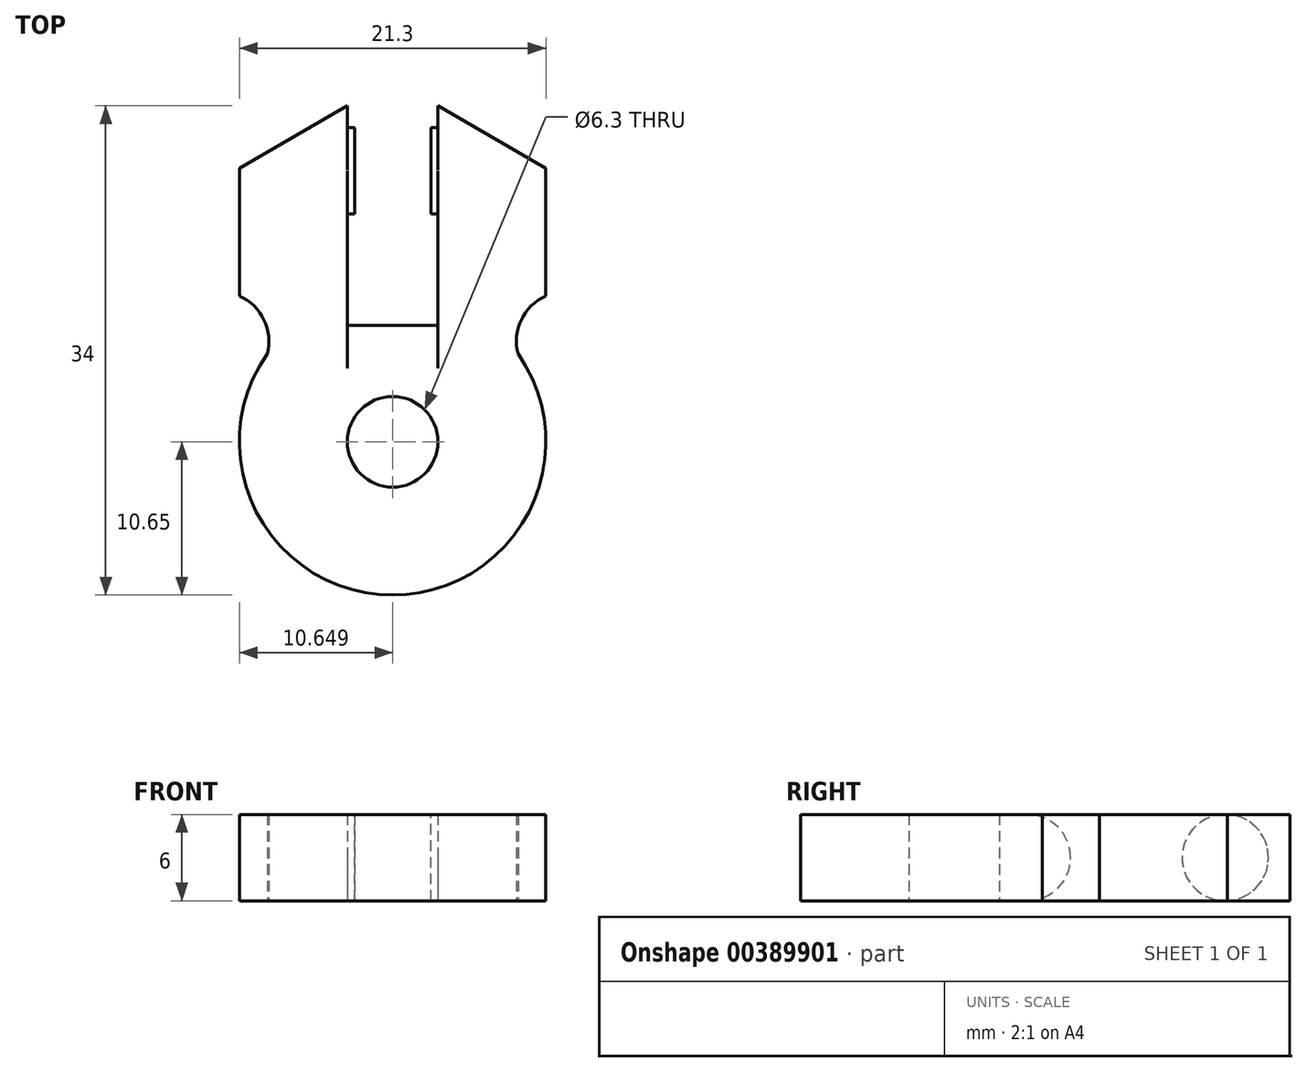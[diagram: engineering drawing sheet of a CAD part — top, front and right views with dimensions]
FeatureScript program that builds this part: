
annotation { "Feature Type Name" : "Feature", "Feature Type Description" : "" }
export const myFeature = defineFeature(function(context is Context, id is Id, definition is map)
    precondition{}
    {
        {
            var Q0;
            Q0=qCreatedBy(makeId("Top.planeOp"),FACE);
            var sketch = newSketch(context, id + "F0", { "sketchPlane" : qUnion([Q0])});
            skCircle(sketch, "E0", {"center": v(27.63, 38) * mm, "radius": 3.15 * mm});
            skArc(sketch, "E1", {"start": v(24.48, 48.16) * mm, "mid": v(27.63, 27.34) * mm, "end": v(30.78, 48.16) * mm});
            skPoint(sketch, "E2", {"position": v(30.78, 46.1) * mm});
            skLineSegment(sketch, "E3", {"start": v(30.78, 46.1) * mm, "end": v(30.78, 61.34) * mm});
            skLineSegment(sketch, "E4", {"start": v(30.78, 46.1) * mm, "end": v(27.63, 46.1) * mm});
            skLineSegment(sketch, "E5.MirrorCS", {"start": v(24.48, 46.1) * mm, "end": v(27.63, 46.1) * mm});
            skLineSegment(sketch, "E6.MirrorCS", {"start": v(24.48, 46.1) * mm, "end": v(24.48, 61.34) * mm});
            skLineSegment(sketch, "E7", {"start": v(16.98, 57) * mm, "end": v(16.98, 48) * mm});
            skLineSegment(sketch, "E8.MirrorCS", {"start": v(38.28, 57) * mm, "end": v(38.28, 48.11) * mm});
            skLineSegment(sketch, "E9", {"start": v(24.48, 61.34) * mm, "end": v(16.98, 57) * mm});
            skLineSegment(sketch, "E10", {"start": v(30.78, 61.34) * mm, "end": v(38.28, 57) * mm});
            skPoint(sketch, "E11.MirrorCS.end.orphan", {"position": v(38.28, 57) * mm});
            skPoint(sketch, "E12.MirrorCS.start.orphan", {"position": v(30.78, 61.34) * mm});
            skArc(sketch, "E13", {"start": v(38.28, 48.11) * mm, "mid": v(36.57, 46.47) * mm, "end": v(36.35, 44.11) * mm});
            skArc(sketch, "E14.MirrorCS", {"start": v(16.98, 48.11) * mm, "mid": v(18.7, 46.47) * mm, "end": v(18.91, 44.11) * mm});
            skSolve(sketch);
        }
        {
            var Q0;
            Q0=qSketchRegion(id+"F0",true);
            extrude(context, id + "F1", {"entities" : qUnion([Q0]), "depth" : 6 * mm});
        }
        {
            var Q0;
            Q0=qCreatedBy(makeId("Right.planeOp"),FACE);
            var sketch = newSketch(context, id + "F2", { "sketchPlane" : qUnion([Q0])});
            skLineSegment(sketch, "E15", {"start": v(61.34, 6) * mm, "end": v(61.34, 0) * mm});
            skLineSegment(sketch, "E16", {"start": v(61.34, 0) * mm, "end": v(57, 0) * mm});
            skLineSegment(sketch, "E17", {"start": v(61.34, 3) * mm, "end": v(59.84, 3) * mm});
            skLineSegment(sketch, "E18", {"start": v(59.84, 3) * mm, "end": v(56.84, 3) * mm});
            skCircle(sketch, "E19", {"center": v(56.84, 3) * mm, "radius": 3 * mm});
            skSolve(sketch);
        }
        {
            var Q0;
            Q0=qSketchRegion(id+"F2",true);
            extrude(context, id + "F3", {"entities" : qUnion([Q0]), "operationType" : NewBodyOperationType.ADD, "depth" : 31 * mm, "hasSecondDirection" : true, "secondDirectionOppositeDirection" : false, "secondDirectionDepth" : 22.4 * mm});
        }
        {
            var Q0;
            Q0=qCreatedBy(makeId("Front.planeOp"),FACE);
            var sketch = newSketch(context, id + "F4", { "sketchPlane" : qUnion([Q0])});
            skLineSegment(sketch, "E20", {"start": v(30.28, 3) * mm, "end": v(30.28, 6.74) * mm});
            skLineSegment(sketch, "E21", {"start": v(30.28, 6.74) * mm, "end": v(24.98, 6.74) * mm});
            skLineSegment(sketch, "E22", {"start": v(24.98, 6.74) * mm, "end": v(24.98, -0.66) * mm});
            skLineSegment(sketch, "E23", {"start": v(24.98, -0.66) * mm, "end": v(30.28, -0.66) * mm});
            skLineSegment(sketch, "E24", {"start": v(30.28, -0.66) * mm, "end": v(30.28, 6.74) * mm});
            skPoint(sketch, "E25.MirrorCS.end.orphan", {"position": v(24.98, 3) * mm});
            skSolve(sketch);
        }
        {
            var Q0;
            {var subQ0=sQuery(id+"F4.wireOp",EDGE,"E21");Q0=makeQuery(id+"F4.imprint","IMPRINT",FACE,{"disambiguationData":[TD([[makeQuery(id+"F4.imprint","IMPRINT",EDGE,{"derivedFrom":subQ0}),1.0]])]});}
            extrude(context, id + "F5", {"entities" : qUnion([Q0]), "operationType" : NewBodyOperationType.REMOVE, "oppositeDirection" : true, "depth" : 63.7 * mm, "hasSecondDirection" : true, "secondDirectionOppositeDirection" : true, "secondDirectionDepth" : 52.7 * mm});
        }
        {
            var Q0;
            Q0=makeQuery(id+"F1.opExtrude","CAP_EDGE",EDGE,{"disambiguationData":[OSD([sQuery(id+"F0.wireOp",EDGE,"E4"),sQuery(id+"F0.wireOp",EDGE,"E5.MirrorCS")])],"isStart":false});
            fillet(context, id + "F6", {"entities" : qUnion([Q0]), "radius" : 3 * mm, "tangentPropagation" : true, "allowEdgeOverflow" : false});
        }
        {
            var Q0;
            Q0=makeQuery(id+"F1.opExtrude","CAP_EDGE",EDGE,{"disambiguationData":[OSD([sQuery(id+"F0.wireOp",EDGE,"E4"),sQuery(id+"F0.wireOp",EDGE,"E5.MirrorCS")])],"isStart":true});
            fillet(context, id + "F7", {"entities" : qUnion([Q0]), "radius" : 3 * mm, "tangentPropagation" : true, "allowEdgeOverflow" : false});
        }
    });
